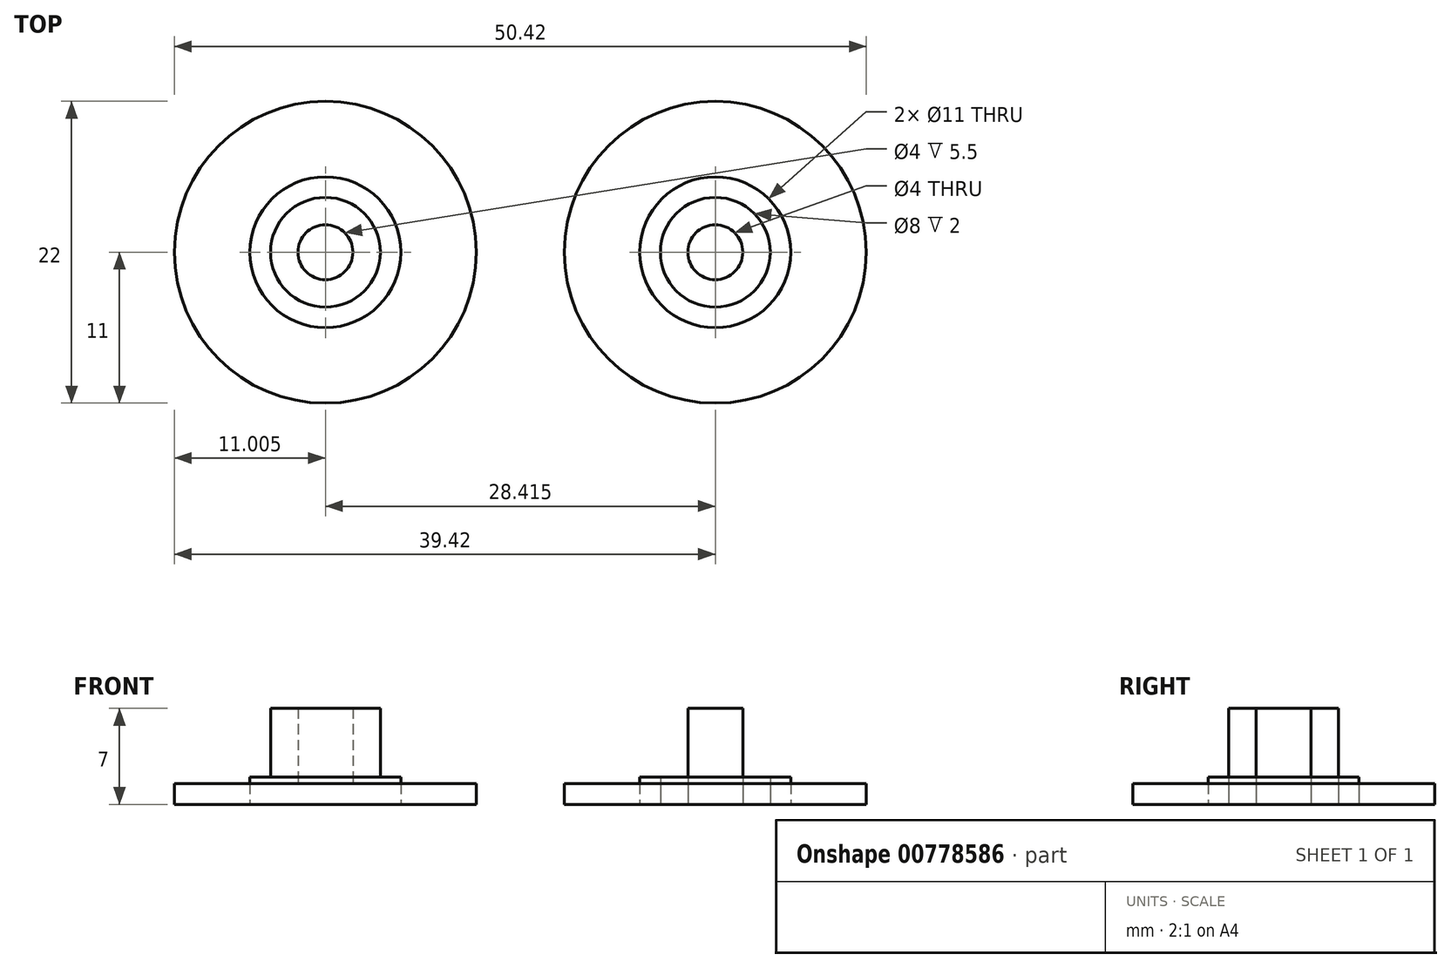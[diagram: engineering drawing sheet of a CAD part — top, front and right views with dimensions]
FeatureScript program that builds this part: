
annotation { "Feature Type Name" : "Feature", "Feature Type Description" : "" }
export const myFeature = defineFeature(function(context is Context, id is Id, definition is map)
    precondition{}
    {
        {
            var Q0;
            Q0=qCreatedBy(makeId("Top.planeOp"),FACE);
            var sketch = newSketch(context, id + "F0", { "sketchPlane" : qUnion([Q0])});
            skCircle(sketch, "E0", {"center": v(0, 0) * mm, "radius": 11 * mm});
            skCircle(sketch, "E1", {"center": v(0, 0) * mm, "radius": 5.5 * mm});
            skCircle(sketch, "E2", {"center": v(0, 0) * mm, "radius": 4 * mm});
            skCircle(sketch, "E3", {"center": v(0, 0) * mm, "radius": 2 * mm});
            skCircle(sketch, "E4", {"center": v(-28.42, 0) * mm, "radius": 11 * mm});
            skCircle(sketch, "E5", {"center": v(-28.42, 0) * mm, "radius": 5.5 * mm});
            skCircle(sketch, "E6", {"center": v(-28.42, 0) * mm, "radius": 4 * mm});
            skCircle(sketch, "E7", {"center": v(-28.42, 0) * mm, "radius": 2 * mm});
            skSolve(sketch);
        }
        {
            var Q0;
            Q0=makeQuery(id+"F0.imprint","IMPRINT",FACE,{"disambiguationData":[TD([[makeQuery(id+"F0.imprint","IMPRINT",EDGE,{"derivedFrom":sQuery(id+"F0.wireOp",EDGE,"E0")}),1.0]])]});
            var Q1;
            Q1=makeQuery(id+"F0.imprint","IMPRINT",FACE,{"disambiguationData":[TD([[makeQuery(id+"F0.imprint","IMPRINT",EDGE,{"derivedFrom":sQuery(id+"F0.wireOp",EDGE,"E4")}),1.0]])]});
            extrude(context, id + "F1", {"entities" : qUnion([Q0, Q1]), "depth" : 1.5 * mm, "offsetDistance" : 25 * mm});
        }
        {
            var Q0;
            Q0=makeQuery(id+"F0.imprint","IMPRINT",FACE,{"disambiguationData":[TD([[makeQuery(id+"F0.imprint","IMPRINT",EDGE,{"derivedFrom":sQuery(id+"F0.wireOp",EDGE,"E1")}),1.0]])]});
            var Q1;
            Q1=makeQuery(id+"F0.imprint","IMPRINT",FACE,{"disambiguationData":[TD([[makeQuery(id+"F0.imprint","IMPRINT",EDGE,{"derivedFrom":sQuery(id+"F0.wireOp",EDGE,"E5")}),1.0]])]});
            extrude(context, id + "F2", {"entities" : qUnion([Q0, Q1]), "depth" : 2 * mm, "offsetDistance" : 25 * mm});
        }
        {
            var Q0;
            Q0=makeQuery(id+"F0.imprint","IMPRINT",FACE,{"disambiguationData":[TD([[makeQuery(id+"F0.imprint","IMPRINT",EDGE,{"derivedFrom":sQuery(id+"F0.wireOp",EDGE,"E6")}),1.0]])]});
            var Q1;
            Q1=makeQuery(id+"F0.imprint","IMPRINT",FACE,{"disambiguationData":[TD([[makeQuery(id+"F0.imprint","IMPRINT",EDGE,{"derivedFrom":sQuery(id+"F0.wireOp",EDGE,"E3")}),1.0]])]});
            extrude(context, id + "F3", {"entities" : qUnion([Q0, Q1]), "operationType" : NewBodyOperationType.ADD, "depth" : 7 * mm, "offsetDistance" : 25 * mm});
        }
        {
            var Q0;
            Q0=makeQuery(id+"F0.imprint","IMPRINT",FACE,{"disambiguationData":[TD([[makeQuery(id+"F0.imprint","IMPRINT",EDGE,{"derivedFrom":sQuery(id+"F0.wireOp",EDGE,"E2")}),1.0]])]});
            extrude(context, id + "F4", {"entities" : qUnion([Q0]), "depth" : 1.5 * mm, "offsetDistance" : 25 * mm});
        }
        {
            var Q0;
            Q0=makeQuery(id+"F0.imprint","IMPRINT",FACE,{"disambiguationData":[TD([[makeQuery(id+"F0.imprint","IMPRINT",EDGE,{"derivedFrom":sQuery(id+"F0.wireOp",EDGE,"E7")}),1.0]])]});
            extrude(context, id + "F5", {"entities" : qUnion([Q0]), "operationType" : NewBodyOperationType.ADD, "depth" : 1.5 * mm, "offsetDistance" : 25 * mm});
        }
    });
